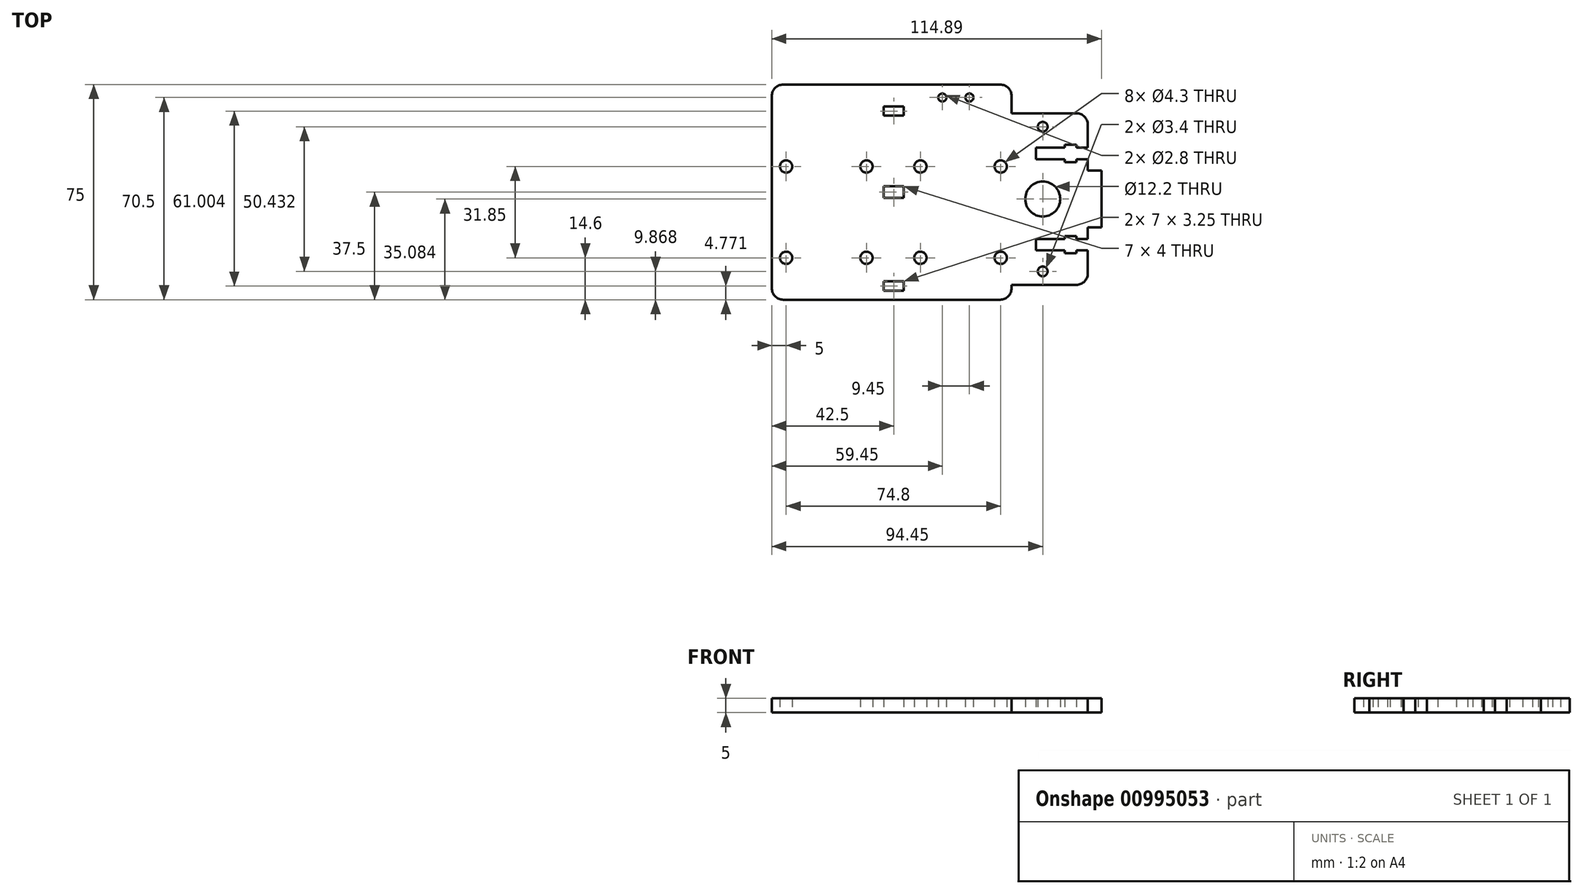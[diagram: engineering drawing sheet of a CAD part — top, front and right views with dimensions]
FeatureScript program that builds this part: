
annotation { "Feature Type Name" : "Feature", "Feature Type Description" : "" }
export const myFeature = defineFeature(function(context is Context, id is Id, definition is map)
    precondition{}
    {
        {
            var Q0;
            Q0=qCreatedBy(makeId("Top.planeOp"),FACE);
            var sketch = newSketch(context, id + "F0", { "sketchPlane" : qUnion([Q0])});
            skLineSegment(sketch, "E0.bottom", {"start": v(4, 0) * mm, "end": v(79.6, 0) * mm});
            skLineSegment(sketch, "E0.top", {"start": v(4, 75) * mm, "end": v(79.6, 75) * mm});
            skLineSegment(sketch, "E0.left", {"start": v(0, 4) * mm, "end": v(0, 71) * mm});
            skLineSegment(sketch, "E0.right", {"start": v(114.89, 25.17) * mm, "end": v(114.89, 45) * mm});
            skPoint(sketch, "E1.visualSharp", {"position": v(0, 75) * mm});
            skArc(sketch, "E1.filletArc", {"start": v(4, 75) * mm, "mid": v(1.17, 73.83) * mm, "end": v(0, 71) * mm});
            skPoint(sketch, "E2.visualSharp", {"position": v(0, 0) * mm});
            skArc(sketch, "E2.filletArc", {"start": v(0, 4) * mm, "mid": v(1.17, 1.17) * mm, "end": v(4, 0) * mm});
            skCircle(sketch, "E3", {"center": v(5, 46.45) * mm, "radius": 2.15 * mm});
            skCircle(sketch, "E4", {"center": v(33, 46.45) * mm, "radius": 2.15 * mm});
            skCircle(sketch, "E5", {"center": v(51.8, 46.45) * mm, "radius": 2.15 * mm});
            skCircle(sketch, "E6", {"center": v(79.8, 46.45) * mm, "radius": 2.15 * mm});
            skCircle(sketch, "E7", {"center": v(5, 14.6) * mm, "radius": 2.15 * mm});
            skCircle(sketch, "E8", {"center": v(33, 14.6) * mm, "radius": 2.15 * mm});
            skCircle(sketch, "E9", {"center": v(51.8, 14.6) * mm, "radius": 2.15 * mm});
            skCircle(sketch, "E10", {"center": v(79.8, 14.6) * mm, "radius": 2.15 * mm});
            skLineSegment(sketch, "E11.bottom", {"start": v(46, 64.15) * mm, "end": v(39, 64.15) * mm});
            skLineSegment(sketch, "E11.top", {"start": v(46, 67.4) * mm, "end": v(39, 67.4) * mm});
            skLineSegment(sketch, "E11.left", {"start": v(46, 64.15) * mm, "end": v(46, 67.4) * mm});
            skLineSegment(sketch, "E11.right", {"start": v(39, 64.15) * mm, "end": v(39, 67.4) * mm});
            skPoint(sketch, "E11.middle", {"position": v(42.5, 65.78) * mm});
            skLineSegment(sketch, "E12.bottom", {"start": v(46, 3.15) * mm, "end": v(39, 3.15) * mm});
            skLineSegment(sketch, "E12.top", {"start": v(46, 6.4) * mm, "end": v(39, 6.4) * mm});
            skLineSegment(sketch, "E12.left", {"start": v(46, 3.15) * mm, "end": v(46, 6.4) * mm});
            skLineSegment(sketch, "E12.right", {"start": v(39, 3.15) * mm, "end": v(39, 6.4) * mm});
            skPoint(sketch, "E12.middle", {"position": v(42.5, 4.77) * mm});
            skCircle(sketch, "E13", {"center": v(59.45, 70.5) * mm, "radius": 1.4 * mm});
            skCircle(sketch, "E14", {"center": v(68.9, 70.5) * mm, "radius": 1.4 * mm});
            skLineSegment(sketch, "E15", {"start": v(83.6, 71) * mm, "end": v(83.6, 65) * mm});
            skLineSegment(sketch, "E16", {"start": v(83.6, 65) * mm, "end": v(106.15, 65) * mm});
            skLineSegment(sketch, "E17", {"start": v(110.15, 61) * mm, "end": v(110.15, 53) * mm});
            skLineSegment(sketch, "E18", {"start": v(110.15, 45) * mm, "end": v(114.89, 45) * mm});
            skLineSegment(sketch, "E19", {"start": v(114.89, 45) * mm, "end": v(114.89, 25.17) * mm});
            skLineSegment(sketch, "E20", {"start": v(114.89, 25.17) * mm, "end": v(110.15, 25.17) * mm});
            skLineSegment(sketch, "E21", {"start": v(110.15, 25.17) * mm, "end": v(110.15, 21.16) * mm});
            skLineSegment(sketch, "E22", {"start": v(106.15, 5.17) * mm, "end": v(83.6, 5.17) * mm});
            skCircle(sketch, "E23", {"center": v(94.45, 60.3) * mm, "radius": 1.7 * mm});
            skCircle(sketch, "E24", {"center": v(94.45, 9.87) * mm, "radius": 1.7 * mm});
            skCircle(sketch, "E25", {"center": v(94.45, 35.08) * mm, "radius": 6.1 * mm});
            skLineSegment(sketch, "E26.bottom", {"start": v(110.15, 53) * mm, "end": v(106.15, 53) * mm});
            skLineSegment(sketch, "E26.top", {"start": v(110.15, 49) * mm, "end": v(106.15, 49) * mm});
            skLineSegment(sketch, "E26.right", {"start": v(92.15, 53) * mm, "end": v(92.15, 49) * mm});
            skLineSegment(sketch, "E27.bottom", {"start": v(106.15, 48) * mm, "end": v(102.15, 48) * mm});
            skLineSegment(sketch, "E27.top", {"start": v(106.15, 54) * mm, "end": v(102.15, 54) * mm});
            skLineSegment(sketch, "E27.left", {"start": v(106.15, 48) * mm, "end": v(106.15, 49) * mm});
            skLineSegment(sketch, "E27.right", {"start": v(102.15, 48) * mm, "end": v(102.15, 49) * mm});
            skPoint(sketch, "E27.middle", {"position": v(104.15, 51) * mm});
            skLineSegment(sketch, "E28.MirrorCS", {"start": v(106.15, 22.16) * mm, "end": v(102.15, 22.16) * mm});
            skLineSegment(sketch, "E29.MirrorCS", {"start": v(106.15, 22.16) * mm, "end": v(106.15, 21.16) * mm});
            skLineSegment(sketch, "E30.MirrorCS", {"start": v(102.15, 22.16) * mm, "end": v(102.15, 21.16) * mm});
            skLineSegment(sketch, "E31.MirrorCS", {"start": v(106.15, 16.16) * mm, "end": v(102.15, 16.16) * mm});
            skLineSegment(sketch, "E32.MirrorCS", {"start": v(92.15, 17.16) * mm, "end": v(92.15, 21.16) * mm});
            skLineSegment(sketch, "E33.MirrorCS", {"start": v(110.15, 17.16) * mm, "end": v(106.15, 17.16) * mm});
            skLineSegment(sketch, "E34.MirrorCS", {"start": v(110.15, 21.16) * mm, "end": v(106.15, 21.16) * mm});
            skLineSegment(sketch, "E35.trimOffspring", {"start": v(83.6, 5.17) * mm, "end": v(83.6, 4) * mm});
            skLineSegment(sketch, "E36.trimOffspring", {"start": v(102.15, 17.16) * mm, "end": v(102.15, 16.16) * mm});
            skLineSegment(sketch, "E37.trimOffspring", {"start": v(102.15, 21.16) * mm, "end": v(92.15, 21.16) * mm});
            skLineSegment(sketch, "E38.trimOffspring", {"start": v(106.15, 17.16) * mm, "end": v(106.15, 16.16) * mm});
            skLineSegment(sketch, "E39.trimOffspring", {"start": v(102.15, 17.16) * mm, "end": v(92.15, 17.16) * mm});
            skLineSegment(sketch, "E40.trimOffspring", {"start": v(102.15, 49) * mm, "end": v(92.15, 49) * mm});
            skLineSegment(sketch, "E41.trimOffspring", {"start": v(102.15, 53) * mm, "end": v(92.15, 53) * mm});
            skLineSegment(sketch, "E42.trimOffspring", {"start": v(102.15, 53) * mm, "end": v(102.15, 54) * mm});
            skLineSegment(sketch, "E43.trimOffspring", {"start": v(106.15, 53) * mm, "end": v(106.15, 54) * mm});
            skLineSegment(sketch, "E44.trimOffspring", {"start": v(110.15, 49) * mm, "end": v(110.15, 45) * mm});
            skLineSegment(sketch, "E45.trimOffspring", {"start": v(110.15, 17.16) * mm, "end": v(110.15, 9.17) * mm});
            skPoint(sketch, "E46.visualSharp", {"position": v(83.6, 75) * mm});
            skArc(sketch, "E46.filletArc", {"start": v(83.6, 71) * mm, "mid": v(82.43, 73.83) * mm, "end": v(79.6, 75) * mm});
            skPoint(sketch, "E47.visualSharp", {"position": v(83.6, 0) * mm});
            skArc(sketch, "E47.filletArc", {"start": v(79.6, 0) * mm, "mid": v(82.43, 1.17) * mm, "end": v(83.6, 4) * mm});
            skPoint(sketch, "E48.visualSharp", {"position": v(110.15, 5.17) * mm});
            skArc(sketch, "E48.filletArc", {"start": v(106.15, 5.17) * mm, "mid": v(108.98, 6.34) * mm, "end": v(110.15, 9.17) * mm});
            skPoint(sketch, "E49.visualSharp", {"position": v(110.15, 65) * mm});
            skArc(sketch, "E49.filletArc", {"start": v(110.15, 61) * mm, "mid": v(108.98, 63.83) * mm, "end": v(106.15, 65) * mm});
            skLineSegment(sketch, "E50.bottom", {"start": v(46, 35.5) * mm, "end": v(39, 35.5) * mm});
            skLineSegment(sketch, "E50.top", {"start": v(46, 39.5) * mm, "end": v(39, 39.5) * mm});
            skLineSegment(sketch, "E50.left", {"start": v(46, 35.5) * mm, "end": v(46, 39.5) * mm});
            skLineSegment(sketch, "E50.right", {"start": v(39, 35.5) * mm, "end": v(39, 39.5) * mm});
            skPoint(sketch, "E50.middle", {"position": v(42.5, 37.5) * mm});
            skPoint(sketch, "E51.orphan", {"position": v(94.45, 5.17) * mm});
            skPoint(sketch, "E52.orphan", {"position": v(42.5, 0) * mm});
            skPoint(sketch, "E53.orphan", {"position": v(42.5, 75) * mm});
            skPoint(sketch, "E54.start.orphan", {"position": v(94.45, 65) * mm});
            skPoint(sketch, "E55.trimOffspring.end.orphan", {"position": v(110.15, 51) * mm});
            skPoint(sketch, "E56.start.orphan", {"position": v(92.15, 51) * mm});
            skSolve(sketch);
        }
        {
            var Q0;
            Q0 = qSketchRegion(id + "F0", true);
            extrude(context, id + "F1", {"entities" : qUnion([Q0]), "depth" : 5 * mm, "offsetDistance" : 25 * mm});
        }
    });
